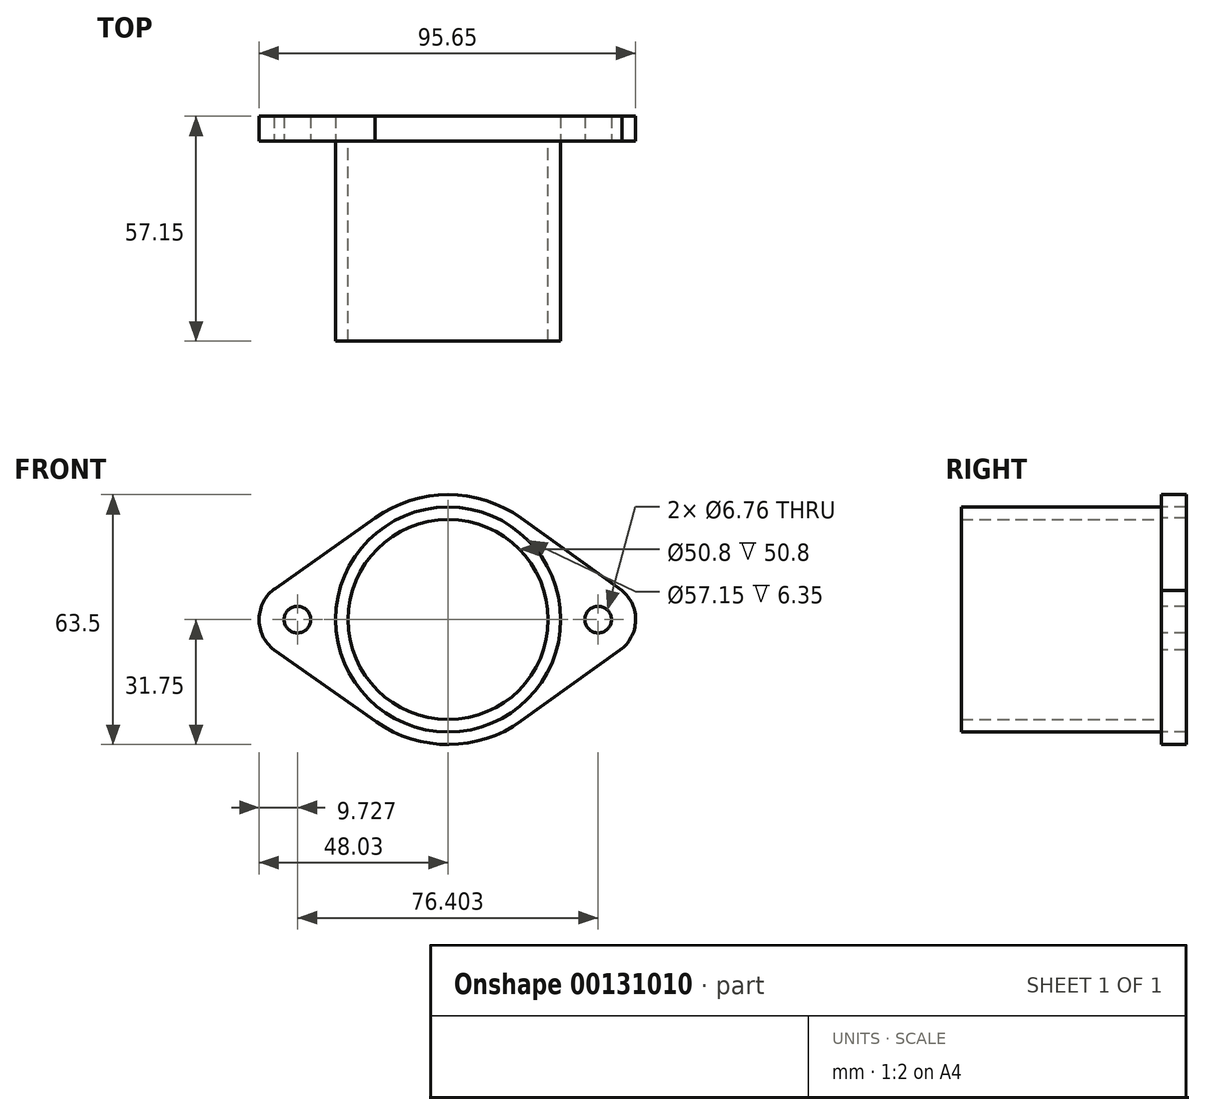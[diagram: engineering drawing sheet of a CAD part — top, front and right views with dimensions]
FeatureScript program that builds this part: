
annotation { "Feature Type Name" : "Feature", "Feature Type Description" : "" }
export const myFeature = defineFeature(function(context is Context, id is Id, definition is map)
    precondition{}
    {
        {
            var Q0;
            Q0=qCreatedBy(makeId("Front.planeOp"),FACE);
            var sketch = newSketch(context, id + "F0", { "sketchPlane" : qUnion([Q0])});
            skCircle(sketch, "E0", {"center": v(0, 0) * mm, "radius": 28.58 * mm});
            skCircle(sketch, "E1", {"center": v(-38.3, 0) * mm, "radius": 3.38 * mm});
            skCircle(sketch, "E2", {"center": v(38.1, 0) * mm, "radius": 3.38 * mm});
            skArc(sketch, "E3", {"start": v(-18.26, -25.97) * mm, "mid": v(0.18, -31.75) * mm, "end": v(18.55, -25.77) * mm});
            skArc(sketch, "E4", {"start": v(-43.9, 7.96) * mm, "mid": v(-48.03, -0.24) * mm, "end": v(-43.5, -8.23) * mm});
            skArc(sketch, "E5", {"start": v(43.66, -7.74) * mm, "mid": v(47.62, 0.3) * mm, "end": v(43.15, 8.07) * mm});
            skLineSegment(sketch, "E6", {"start": v(-18.58, 25.75) * mm, "end": v(-43.9, 7.96) * mm});
            skLineSegment(sketch, "E7", {"start": v(18.54, 25.78) * mm, "end": v(44.15, 7.36) * mm});
            skLineSegment(sketch, "E8", {"start": v(-18.26, -25.97) * mm, "end": v(-44.29, -7.67) * mm});
            skLineSegment(sketch, "E9", {"start": v(18.55, -25.77) * mm, "end": v(43.66, -7.74) * mm});
            skArc(sketch, "E10.trimOffspring", {"start": v(18.54, 25.78) * mm, "mid": v(-0.02, 31.75) * mm, "end": v(-18.58, 25.75) * mm});
            skSolve(sketch);
        }
        {
            var Q0;
            Q0=makeQuery(id+"F0.imprint","IMPRINT",FACE,{"disambiguationData":[TD([[makeQuery(id+"F0.imprint","IMPRINT",EDGE,{"derivedFrom":sQuery(id+"F0.wireOp",EDGE,"E0")}),-1.0]])]});
            extrude(context, id + "F1", {"entities" : qUnion([Q0]), "oppositeDirection" : true, "depth" : 6.35 * mm});
        }
        {
            var Q0;
            Q0=qCreatedBy(makeId("Front.planeOp"),FACE);
            var sketch = newSketch(context, id + "F2", { "sketchPlane" : qUnion([Q0])});
            skCircle(sketch, "E11", {"center": v(0, 0) * mm, "radius": 25.4 * mm});
            skCircle(sketch, "E12", {"center": v(0, 0) * mm, "radius": 28.58 * mm});
            skSolve(sketch);
        }
        {
            var Q0;
            Q0 = qSketchRegion(id + "F2", true);
            extrude(context, id + "F3", {"entities" : qUnion([Q0]), "depth" : 50.8 * mm});
        }
    });
